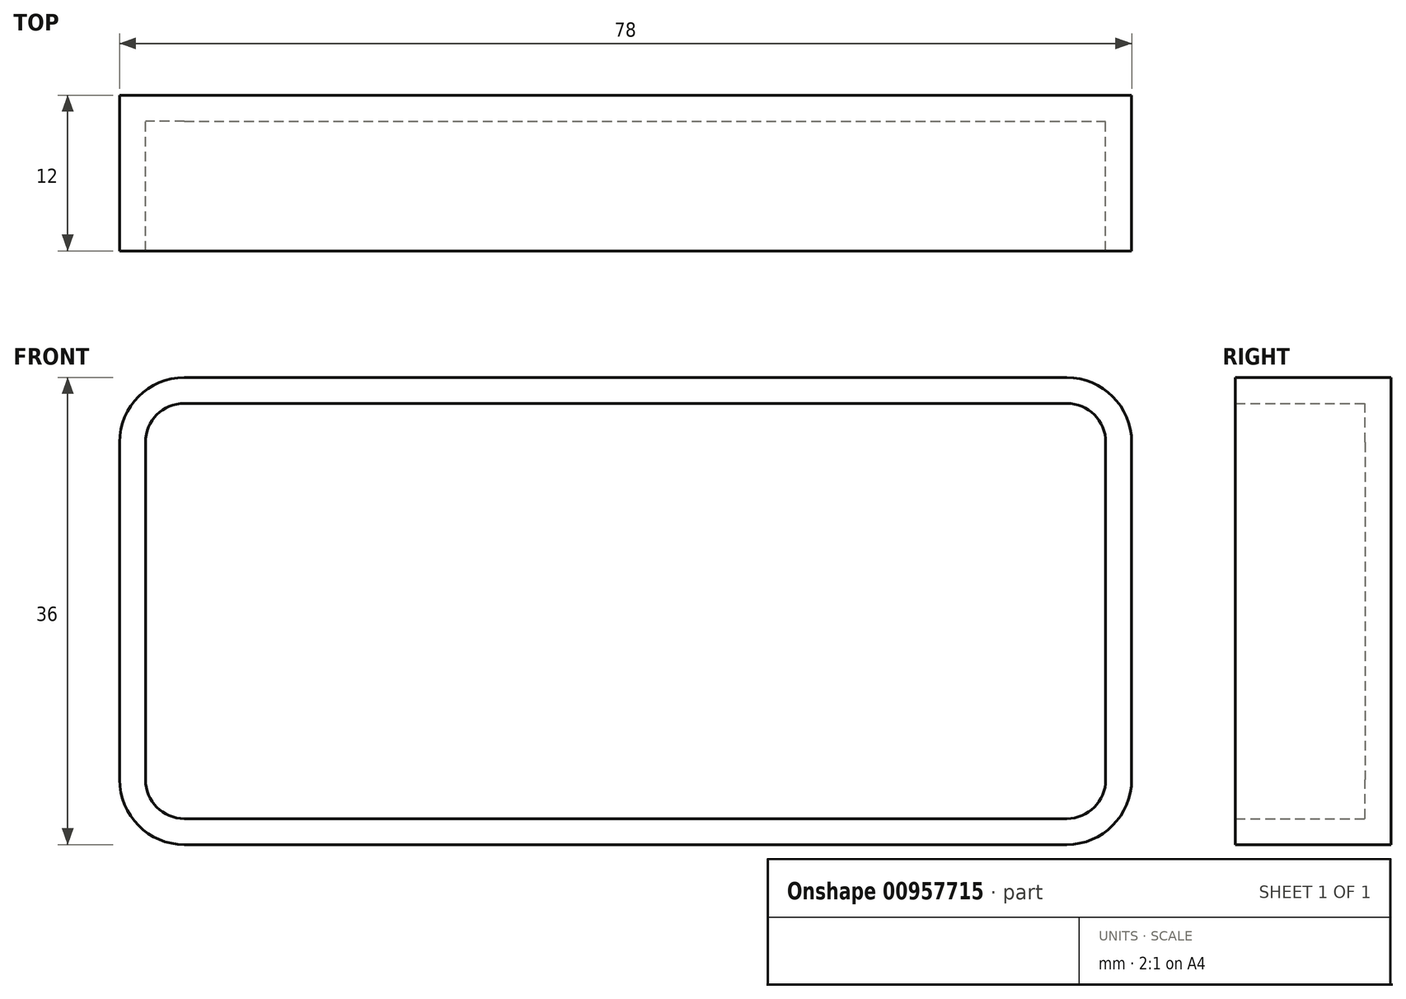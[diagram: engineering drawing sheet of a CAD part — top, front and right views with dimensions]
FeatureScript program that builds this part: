
annotation { "Feature Type Name" : "Feature", "Feature Type Description" : "" }
export const myFeature = defineFeature(function(context is Context, id is Id, definition is map)
    precondition{}
    {
        {
            var Q0;
            Q0=qCreatedBy(makeId("Front.planeOp"),FACE);
            var sketch = newSketch(context, id + "F0", { "sketchPlane" : qUnion([Q0])});
            skLineSegment(sketch, "E0.bottom", {"start": v(-35.52, 5.75) * mm, "end": v(42.48, 5.75) * mm});
            skLineSegment(sketch, "E0.top", {"start": v(-35.52, -30.25) * mm, "end": v(42.48, -30.25) * mm});
            skLineSegment(sketch, "E0.left", {"start": v(-35.52, 5.75) * mm, "end": v(-35.52, -30.25) * mm});
            skLineSegment(sketch, "E0.right", {"start": v(42.48, 5.75) * mm, "end": v(42.48, -30.25) * mm});
            skSolve(sketch);
        }
        {
            var Q0;
            Q0 = qSketchRegion(id + "F0", true);
            extrude(context, id + "F1", {"entities" : qUnion([Q0]), "depth" : 12 * mm, "offsetDistance" : 25 * mm});
        }
        {
            var Q0;
            Q0=makeQuery(id+"F1.opExtrude","SWEPT_EDGE",EDGE,{"disambiguationData":[OSD([sQuery(id+"F0.wireOp",EDGE,"E0.bottom"),sQuery(id+"F0.wireOp",EDGE,"E0.left")])]});
            var Q1;
            Q1=makeQuery(id+"F1.opExtrude","SWEPT_EDGE",EDGE,{"disambiguationData":[OSD([sQuery(id+"F0.wireOp",EDGE,"E0.bottom"),sQuery(id+"F0.wireOp",EDGE,"E0.right")])]});
            var Q2;
            Q2=makeQuery(id+"F1.opExtrude","SWEPT_EDGE",EDGE,{"disambiguationData":[OSD([sQuery(id+"F0.wireOp",EDGE,"E0.top"),sQuery(id+"F0.wireOp",EDGE,"E0.right")])]});
            var Q3;
            Q3=makeQuery(id+"F1.opExtrude","SWEPT_EDGE",EDGE,{"disambiguationData":[OSD([sQuery(id+"F0.wireOp",EDGE,"E0.top"),sQuery(id+"F0.wireOp",EDGE,"E0.left")])]});
            fillet(context, id + "F2", {"entities" : qUnion([Q0, Q1, Q2, Q3]), "radius" : 5 * mm, "tangentPropagation" : true, "allowEdgeOverflow" : false});
        }
        {
            var Q0;
            Q0=makeQuery(id+"F1.opExtrude","CAP_FACE",FACE,{"disambiguationData":[OSD([sQuery(id+"F0.wireOp",EDGE,"E0.bottom"),sQuery(id+"F0.wireOp",EDGE,"E0.top"),sQuery(id+"F0.wireOp",EDGE,"E0.left"),sQuery(id+"F0.wireOp",EDGE,"E0.right")])],"isStart":false});
            shell(context, id + "F3", {"entities" : qUnion([Q0]), "thickness" : 2 * mm});
        }
    });
